# Revit family: ledsparrow-e_15w-dim-830_840_850_523003011600_06be
name_source: partatom
category: Lighting Fixtures
units: mm (PartAtom-declared; Revit-internal decimal feet)

## family parameters
Cut with Voids When Loaded = No
Host = Face
Light Source = No
Part Type = Normal
Room Calculation Point = No
Round Connector Dimension = Use Diameter
Shared = No

## types (1)
- LEDSparrow-E 15W-DIM-830/840/850 (1 x LED, 1000 lm, 3000)
    Apparent Load = 15 VA
    Approval mark = CE
    CIE Flux Codes = 38 73 95 100 100
    Color Rendering = 80
    Color Temperature = 3000
    Control Gear = Electronic ballast
    Default Elevation = 1800 mm
    Description = Modern design desk lamp with comfortable light. Touch-button control for dimming and CCT-change. Professional anti-glare, honeycomb lens . Indirect background lighting for increased comfort . Various scenes/features to enhance ease of use.
    Frequency = 60 Hz
    Height = 410 mm
    Lamp = 1 x LED
    Lamp Light Flux = 1000 lm
    Lamp count = 1
    Length = 405 mm
    Luminous efficacy = 67 lm/W
    Manufacturer = OPPLE
    ModVariant = No
    Model = 523003011600
    Mounting Place = Table
    Mounting Type = Freestanding
    Number of Poles = 1
    OnlyDefault = Yes
    Power Factor = 1
    Product Name = LEDSparrow-E 15W-DIM-830/840/850
    Product group = Desk luminaire
    ProductGroupID = 21
    Protection Class = Protection class II
    Protection Degree = IP 20
    RLX_Detail_Level = 1
    RlxData = <blob elided: 131445 chars, md5=1a1ccc0a>
    Socket = socket
    Standby Power = 0 W
    System Light Flux = 1000 lm
    System Power = 15 W
    Type Comments = Product without accessories
    Type Image = web_sparrow.jpg
    URL = http://relux.com
    VarID = ---
    Voltage = 230 V
    Voltage Range = 220-240 V
    Weight = 0.00 kg
    Width = 120 mm

## geometry (parser evidence)
native form markers: Blend x4, Sweep x13
no freeform markers — native parametric forms only
